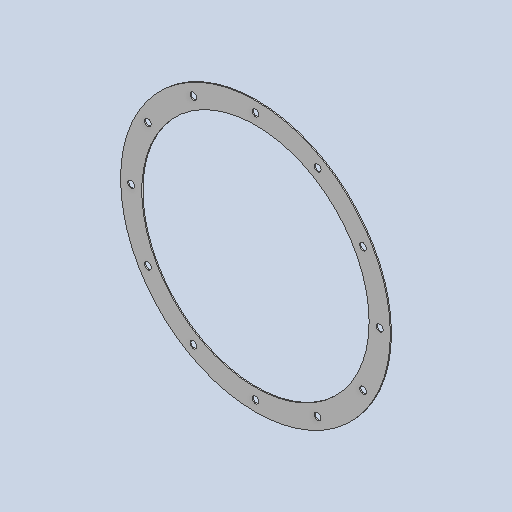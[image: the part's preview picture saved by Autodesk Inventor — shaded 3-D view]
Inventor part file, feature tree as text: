
AUTODESK INVENTOR PART (.ipt)
format: ipt  version: 2025 (Build 290162010, 162A)  size: 298,496 bytes
history: native  units: mm
features: sketch x2, other x2, sheet_metal_op x1, pattern_circular x1
ambient origin geometry x8: Origin, YZ Plane, XZ Plane, XY Plane, X Axis, Y Axis, Z Axis, Center Point
bodies: Solid1 (feature_tree)
feature tree (6):
  sheet_metal_op  "Face1"
  pattern_circular  "Circular Pattern1"  [2 undecoded]
  sketch  "Sketch1"  dims[d15=2.0mm]
  other  "Plate1"
  sketch  "Sketch2"  dims[d31=508.0mm d32=428.0mm d33=13.0mm d34=2.0mm d35=0.0mm d36=120.0mm d37=360.0deg]
  other  "Cut1"
note: 2 required parameter values undecoded (feature->parameter linkage not recoverable at this tier; creation-order binding heuristic only, values carry confidence <= 0.55)
